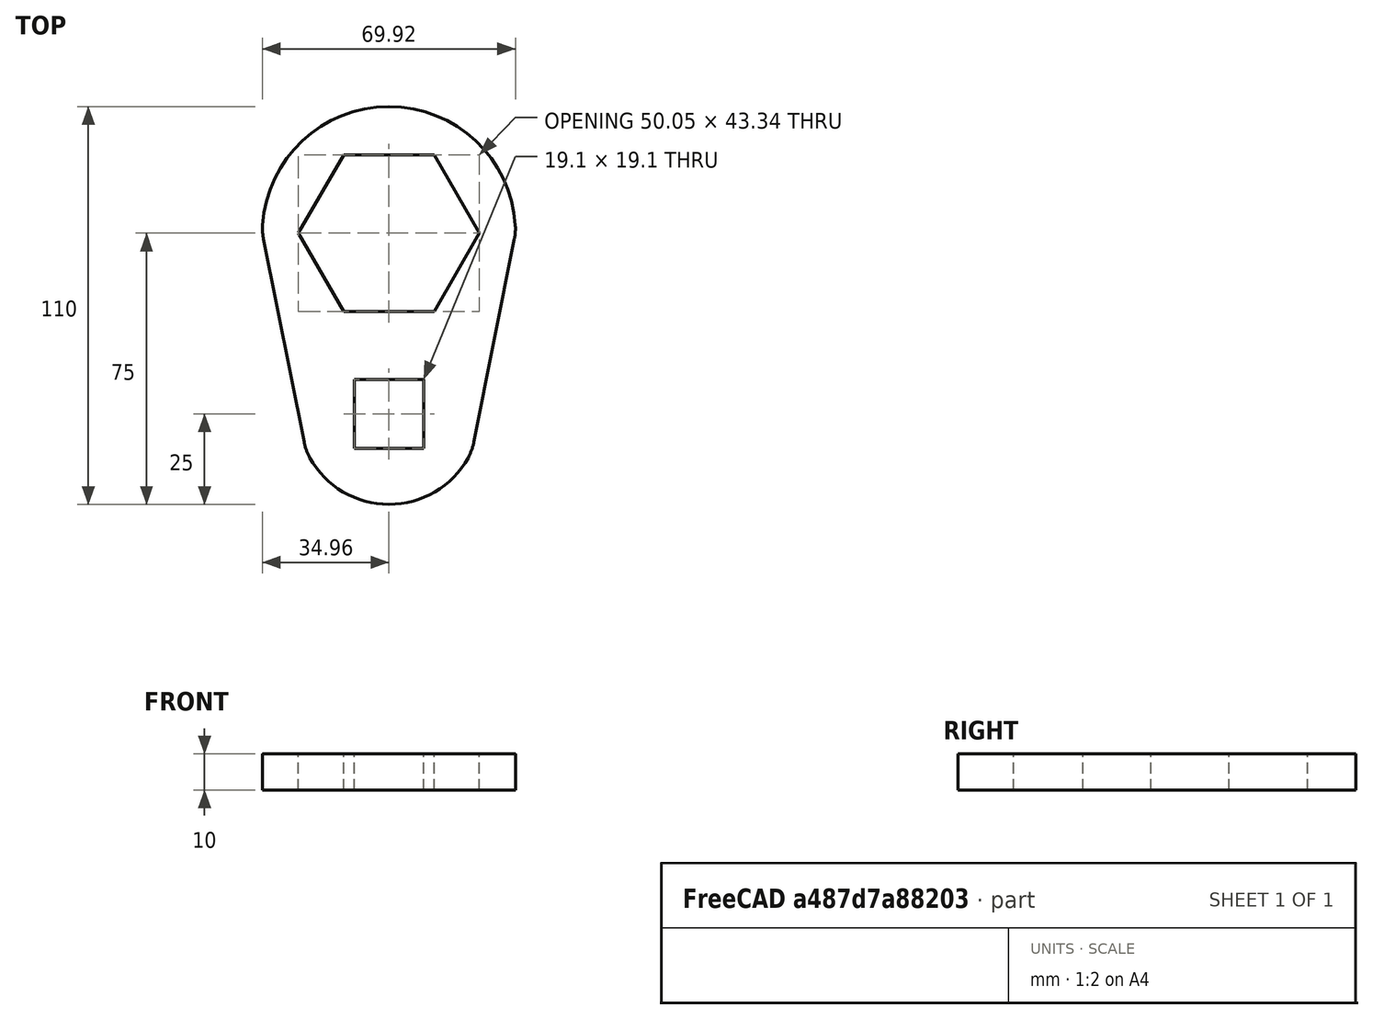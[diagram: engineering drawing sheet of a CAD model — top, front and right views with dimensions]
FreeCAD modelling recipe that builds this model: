
FCSTD DOCUMENT  (FreeCAD 0.18R16131 (Git))
Label: transmission wrench 50 19 w fea
License: All rights reserved
LicenseURL: http://en.wikipedia.org/wiki/All_rights_reserved
objects: Fem::FemMeshObjectPython×2, Sketcher::SketchObject×1, PartDesign::Pad×1, PartDesign::Fillet×1, PartDesign::Body×1, Fem::FemSolverObjectPython×1, App::MaterialObjectPython×1, Fem::ConstraintFixed×1, Fem::ConstraintForce×1, Fem::FemResultObjectPython×1, Fem::FemAnalysis×1
note: 5 computed .brp shape members not serialized (recipe doc carries the construction recipe); baked Part::Feature solids carry a one-line shape summary decoded from their .brp

FEATURE [Sketcher::SketchObject] Sketch
  MapMode = 5
  Support = -> [XY_Plane]
  expr: Constraints[29] = 25.4 * 0.75 + 0.05
  sketch-geometry (17):
    g0: LineSegment StartX=-25.025 StartY=0 StartZ=0 EndX=-12.5125 EndY=-21.6723 EndZ=0
    g1: LineSegment StartX=-12.5125 StartY=-21.6723 StartZ=0 EndX=12.5125 EndY=-21.6723 EndZ=0
    g2: LineSegment StartX=12.5125 StartY=-21.6723 StartZ=0 EndX=25.025 EndY=0 EndZ=0
    g3: LineSegment StartX=25.025 StartY=0 StartZ=0 EndX=12.5125 EndY=21.6723 EndZ=0
    g4: LineSegment StartX=12.5125 StartY=21.6723 StartZ=0 EndX=-12.5125 EndY=21.6723 EndZ=0
    g5: LineSegment StartX=-12.5125 StartY=21.6723 StartZ=0 EndX=-25.025 EndY=0 EndZ=0
    g6: Circle [constr] CenterX=0 CenterY=0 CenterZ=0 NormalX=0 NormalY=0 NormalZ=1 AngleXU=0 Radius=25.025
    g7: LineSegment StartX=9.55 StartY=-59.55 StartZ=0 EndX=9.55 EndY=-40.45 EndZ=0
    g8: LineSegment StartX=9.55 StartY=-40.45 StartZ=0 EndX=-9.55 EndY=-40.45 EndZ=0
    g9: LineSegment StartX=-9.55 StartY=-40.45 StartZ=0 EndX=-9.55 EndY=-59.55 EndZ=0
    g10: LineSegment StartX=-9.55 StartY=-59.55 StartZ=0 EndX=9.55 EndY=-59.55 EndZ=0
    g11: Circle [constr] CenterX=0 CenterY=-50 CenterZ=0 NormalX=0 NormalY=0 NormalZ=1 AngleXU=0 Radius=13.5057
    g12: ArcOfCircle CenterX=0 CenterY=0 CenterZ=0 NormalX=0 NormalY=0 NormalZ=1 AngleXU=0 Radius=35 StartAngle=0 EndAngle=3.14159
    g13: ArcOfCircle CenterX=0 CenterY=-50 CenterZ=0 NormalX=0 NormalY=0 NormalZ=1 AngleXU=0 Radius=25 StartAngle=3.53355 EndAngle=5.89123
    g14: LineSegment StartX=-35 StartY=0 StartZ=0 EndX=-23.1041 EndY=-59.55 EndZ=0
    g15: LineSegment StartX=23.1041 StartY=-59.55 StartZ=0 EndX=35 EndY=0 EndZ=0
    g16: LineSegment [constr] StartX=-23.1041 StartY=-59.55 StartZ=0 EndX=23.1041 EndY=-59.55 EndZ=0
  constraints (44):
    c: Coincident(g0,g1)
    c: Coincident(g1,g2)
    c: Coincident(g2,g3)
    c: Coincident(g3,g4)
    c: Coincident(g4,g5)
    c: Coincident(g5,g0)
    c: Equal(g0, g1-g5) x5
    c: PointOnObject(g0,g6)
    c: PointOnObject(g1,g6)
    c: PointOnObject(g2,g6)
    c: PointOnObject(g3,g6)
    c: Symmetric(g0,g2,g-1)
    c: Coincident(g7,g8)
    c: Coincident(g8,g9)
    c: Coincident(g9,g10)
    c: Coincident(g10,g7)
    c: Equal(g7,g8)
    c: Equal(g7,g9)
    c: Equal(g7,g10)
    c: PointOnObject(g7,g11)
    c: PointOnObject(g8,g11)
    c: PointOnObject(g9,g11)
    c: PointOnObject(g10,g11)
    c: PointOnObject(g11,g-2)
    c: Parallel(g8,g-1)
    c: DistanceX(g9,g7) = 19.1
    c: DistanceY(g11,g-1) = 50
    c: PointOnObject(g12,g-1)
    c: PointOnObject(g12,g-1)
    c: Coincident(g14,g12)
    c: Coincident(g15,g12)
    c: Coincident(g12,g-1)
    c: Radius(g12) = 35
    c: Radius(g13) = 25
    c: Coincident(g15,g13)
    c: Coincident(g13,g14)
    c: Coincident(g13,g11)
    c: Coincident(g13,g16)
    c: Coincident(g16,g13)
    c: Parallel(g16,g-1)
    c: PointOnObject(g7,g16)
    c: Coincident(g6,g12)
    c: PointOnObject(g0,g-1)
    c: DistanceX(g0,g2) = 50.05
FEATURE [PartDesign::Pad] Pad
  Length = 10
  Length2 = 100
  Profile = -> Sketch
  Type = 0
FEATURE [PartDesign::Fillet] Fillet
  Base = -> Pad [Edge2,Edge5,Edge8,Edge1]
  BaseFeature = -> Pad
  Radius = 15
FEATURE [PartDesign::Body] Body
  Group = -> [Sketch,Pad,Fillet]
  Origin = -> Origin
  Tip = -> Fillet
FEATURE [Fem::FemSolverObjectPython] CalculiXccxTools  # FEM object (typed FeaturePython)
  AnalysisType = 0
  BeamShellResultOutput3D = false
  EigenmodeHighLimit = 1000000
  EigenmodeLowLimit = 0
  EigenmodesCount = 10
  GeometricalNonlinearity = 0
  IterationsControlParameterCutb = 0.25,0.5,0.75,0.85,,,1.5,
  IterationsControlParameterIter = 4,8,9,200,10,400,,200,,
  IterationsControlParameterTimeUse = false
  IterationsThermoMechMaximum = 200
  IterationsUserDefinedIncrementations = false
  IterationsUserDefinedTimeStepLength = false
  MaterialNonlinearity = 0
  MatrixSolverType = 0
  SplitInputWriter = false
  ThermoMechSteadyState = true
  TimeEnd = 1
  TimeInitialStep = 1
FEATURE [Fem::FemMeshObjectPython] FEMMeshGmsh  # FEM object (typed FeaturePython)
  Algorithm2D = 0
  Algorithm3D = 0
  CharacteristicLengthMax = 0
  CharacteristicLengthMin = 0
  CoherenceMesh = true
  ElementDimension = 0
  ElementOrder = 1
  GeometryTolerance = 1e-06
  GroupsOfNodes = false
  HighOrderOptimize = false
  OptimizeNetgen = false
  OptimizeStd = true
  Part = -> Fillet
  RecombineAll = false
FEATURE [App::MaterialObjectPython] SolidMaterial  # material (typed FeaturePython)
  Category = 0
  Material = Density=7900 kg/m^3,Description=Standard steel material for CalculiX sample calculations,Father=Metal,Name=CalculiX-Steel,PoissonRatio=0.3,+4 more (map truncated)
FEATURE [Fem::ConstraintFixed] FemConstraintFixed
  NormalDirection = (0.866025,-0.5,0)
  Normals = (72) [(0.866025,-0.5,0),(0.866025,-0.5,0),(0.866025,-0.5,0),(0.866025,-0.5,0),(0.866025,-0.5,0),(0.866025,-0.5,0),(0.866025,-0.5,0),(0.866025,-0.5,0),+64 more]
  Points = (72) [(-12.5125,21.6723,10),(-16.6833,14.4482,10),(-20.8542,7.2241,10),(-25.025,0,10),(-12.5125,21.6723,5),(-16.6833,14.4482,5),(-20.8542,7.2241,5),+65 more]
  References = -> [Fillet]
FEATURE [Fem::ConstraintForce] FemConstraintForce
  DirectionVector = (-1,3e-16,0)
  Force = 8300
  NormalDirection = (1,-3e-16,0)
  Points = (9) [(-9.55,-40.45,10),(-9.55,-50,10),(-9.55,-59.55,10),(-9.55,-40.45,5),(-9.55,-50,5),(-9.55,-59.55,5),(-9.55,-40.45,0),(-9.55,-50,0),(-9.55,-59.55,0)]
  References = -> [Fillet]
  Reversed = true
FEATURE [Fem::FemMeshObjectPython] Result_mesh  # FEM object (typed FeaturePython)
FEATURE [Fem::FemResultObjectPython] CalculiX_static_results  # FEM object (typed FeaturePython)
  DisplacementLengths = [0.000541003,0.000792251,0.000539037,0.000791548,0.000658873,0.000968839,0.0172717,0.0224491,0.0195908,0.0231616,0,0,0,0,0,0,0.0227149,0.0187461,0.00830627,0.00518628,0.000657746,0.000968466,0.0172886,0.0224015,0.0195861,0.023118,0,0,0,0,0,+1033 more]
  DisplacementVectors = (1064) [(-5.33322e-05,-0.000536905,3.96544e-05),(-7.66056e-05,0.000786326,-5.9034e-05),(-5.45113e-05,-0.000534882,-3.86123e-05),+1061 more]
  Eigenmode = 0
  EigenmodeFrequency = 0
  MaxShear = [3.01465,4.27274,2.88756,4.35935,3.40124,4.90312,2.01432,23.7436,5.98796,21.8757,1.0563,10.2318,0.771205,6.68856,17.0957,17.4928,27.8962,35.6542,56.1547,20.9514,3.37025,4.97338,1.515,23.6502,6.19238,21.2053,1.07145,10.4805,0.773178,7.28105,+1034 more]
  Mesh = -> Result_mesh
  NodeNumbers = [1,2,3,4,5,6,7,8,9,10,11,12,13,14,15,16,17,18,19,20,21,22,23,24,25,26,27,28,29,30,31,32,33,34,35,36,37,38,39,40,41,42,43,44,45,46,47,48,49,50,51,52,53,54,55,56,57,58,59,60,61,62,63,64,65,66,67,68,69,+995 more]
  PrincipalMax = [5.84144,-0.0586111,5.73839,-0.0287798,6.47583,0.485636,2.39865,47.1674,0.335509,42.2369,1.02244,8.30732,0.796218,7.38805,21.1434,18.1629,3.2723,79.6171,123.704,-5.8547,6.51556,0.359686,1.79552,46.9869,0.52255,42.0385,0.949378,7.96087,+1036 more]
  PrincipalMed = [0.078408,-0.147545,0.0234927,-0.117487,-0.0910644,0.197147,-0.339898,0.825178,-0.221169,0.566717,0.0230508,-0.569579,-0.0116672,0.225948,1.52744,0.428465,-5.62084,20.6865,19.387,-15.1015,-0.17767,0.280115,-0.21386,1.33975,0.325913,+1039 more]
  PrincipalMin = [-0.187858,-8.60409,-0.0367265,-8.74748,-0.326656,-9.32061,-1.62999,-0.31969,-11.6404,-1.51455,-1.09016,-12.1562,-0.746192,-5.98908,-13.048,-16.8228,-52.5202,8.30877,11.3942,-47.7576,-0.224936,-9.58708,-1.23449,-0.313495,-11.8622,-0.372115,+1038 more]
  ResultType = Fem::FemResultMechanical
  Stats = [-0.0229264,-0.00747177,0.000111913,-0.0058489,0.000301846,0.00767715,-0.000750888,-2.32283e-06,0.000772971,0,0.00789472,0.0231616,0.113184,23.1522,117.618,-14.3354,13.8126,127.7,-56.4948,-0.392327,29.7824,-80.1565,-11.1567,17.3018,+15 more]
  StrainVectors = (1064) [(-9.32003e-06,2.79382e-05,-7.70014e-06),(1.18922e-05,-4.06435e-05,1.19698e-05),(-8.3833e-06,2.73353e-05,-8.04699e-06),+1061 more]
  StressValues = [5.90068,8.50136,5.74525,8.67468,6.68781,9.66523,3.56328,46.9252,11.7075,42.7489,1.83045,17.7737,1.33627,11.5946,29.7177,30.2995,51.9203,65.9959,108.534,38.1298,6.71699,9.90722,2.67023,46.4958,12.2876,42.2019,1.85966,18.2204,1.34155,12.6785,+1034 more]
  StressVectors = (1064) [(-0.182775,5.83587,0.0788993),(-0.112081,-8.59862,-0.0995421),(-0.0330346,5.7369,0.0212927),(-0.0511342,-8.73907,-0.10354),+1060 more]
  Time = 0
FEATURE [Fem::FemAnalysis] Analysis
  Group = -> [CalculiXccxTools,FEMMeshGmsh,SolidMaterial,FemConstraintFixed,FemConstraintForce,CalculiX_static_results]
